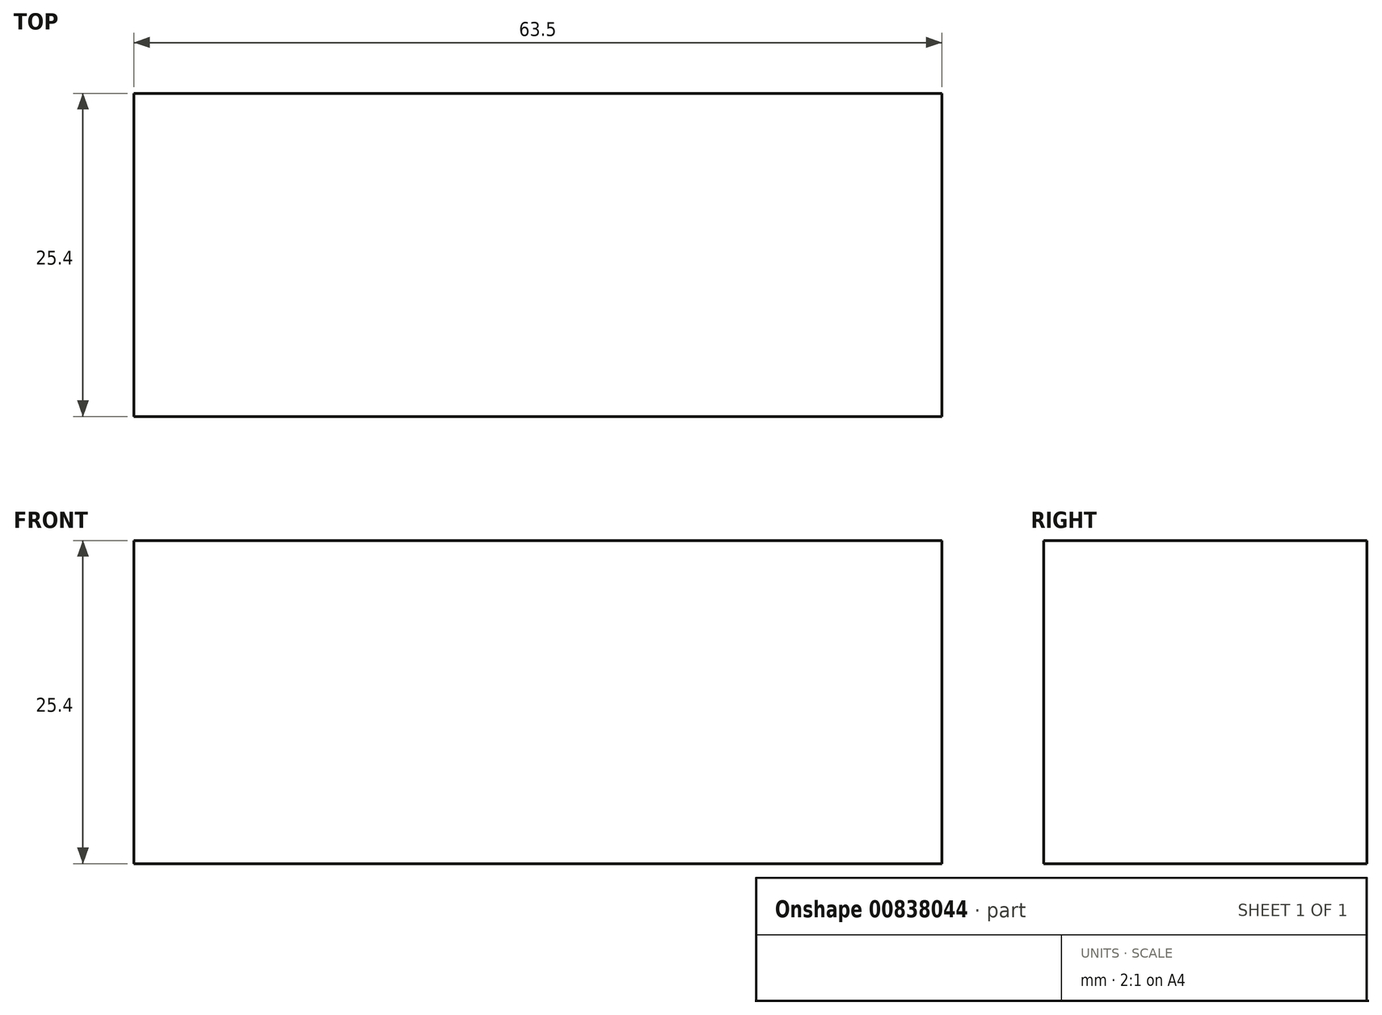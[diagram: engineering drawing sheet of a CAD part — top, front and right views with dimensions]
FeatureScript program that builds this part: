
annotation { "Feature Type Name" : "Feature", "Feature Type Description" : "" }
export const myFeature = defineFeature(function(context is Context, id is Id, definition is map)
    precondition{}
    {
        {
            var Q0;
            Q0=qCreatedBy(makeId("Top.planeOp"),FACE);
            var sketch = newSketch(context, id + "F0", { "sketchPlane" : qUnion([Q0])});
            skLineSegment(sketch, "E0.bottom", {"start": v(-33.82, 4.57) * mm, "end": v(29.68, 4.57) * mm});
            skLineSegment(sketch, "E0.top", {"start": v(-33.82, 29.97) * mm, "end": v(29.68, 29.97) * mm});
            skLineSegment(sketch, "E0.left", {"start": v(-33.82, 4.57) * mm, "end": v(-33.82, 29.97) * mm});
            skLineSegment(sketch, "E0.right", {"start": v(29.68, 4.57) * mm, "end": v(29.68, 29.97) * mm});
            skSolve(sketch);
        }
        {
            var Q0;
            Q0=makeQuery(id+"F0.imprint","IMPRINT",FACE,{"disambiguationData":[TD([[makeQuery(id+"F0.imprint","IMPRINT",EDGE,{"derivedFrom":sQuery(id+"F0.wireOp",EDGE,"E0.bottom")}),1.0]])]});
            extrude(context, id + "F1", {"entities" : qUnion([Q0]), "depth" : 25.4 * mm, "offsetDistance" : 25.4 * mm});
        }
    });
